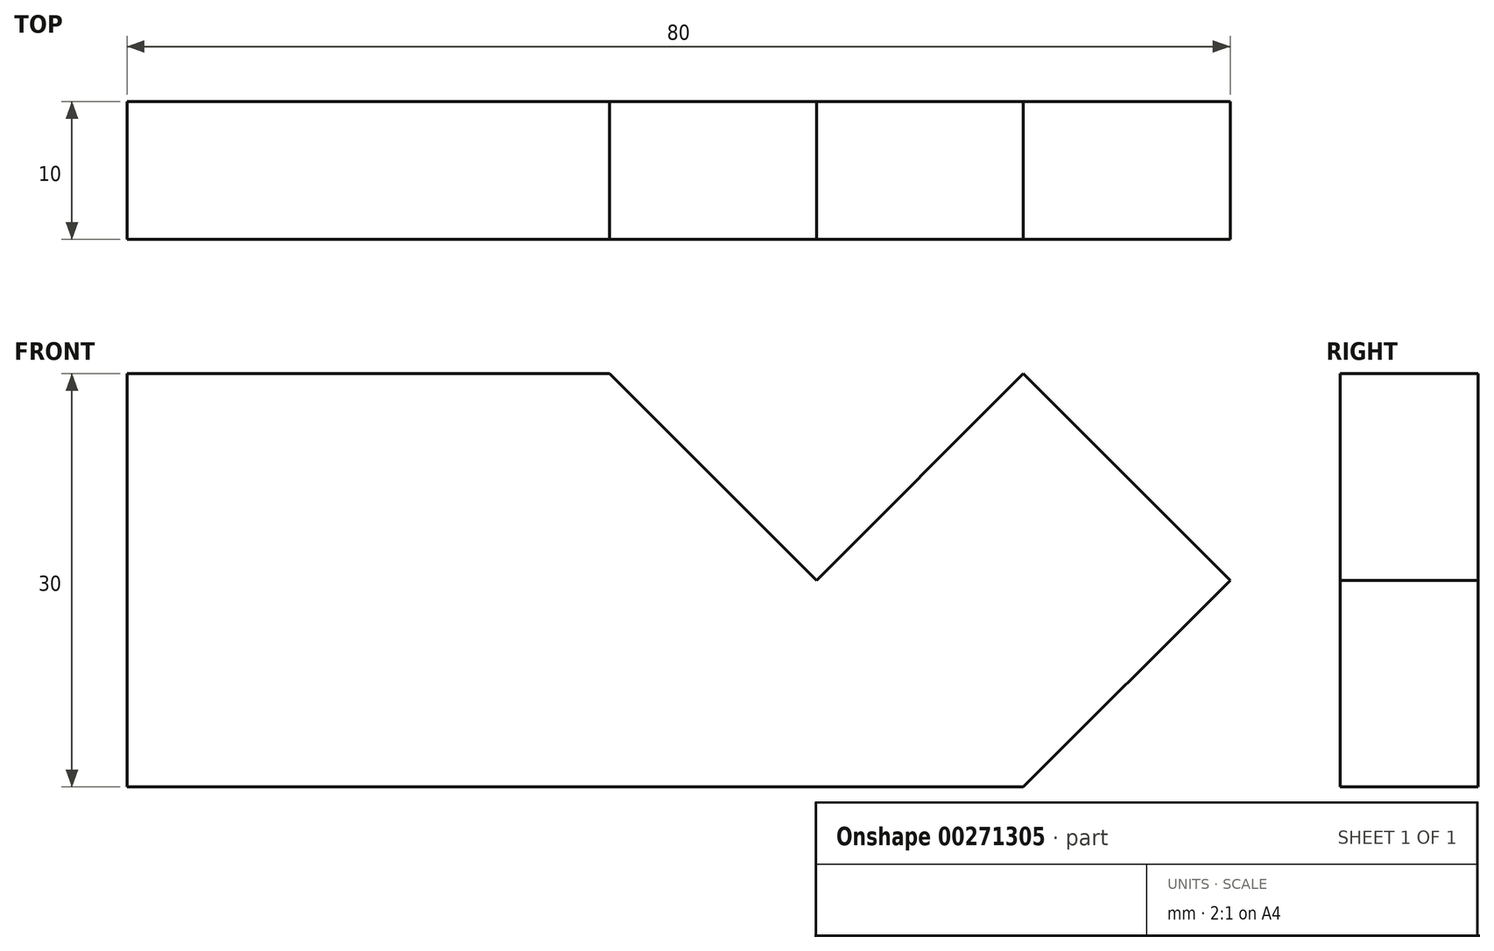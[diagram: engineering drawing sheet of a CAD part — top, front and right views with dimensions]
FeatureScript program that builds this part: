
annotation { "Feature Type Name" : "Feature", "Feature Type Description" : "" }
export const myFeature = defineFeature(function(context is Context, id is Id, definition is map)
    precondition{}
    {
        {
            var Q0;
            Q0=qCreatedBy(makeId("Front.planeOp"),FACE);
            var sketch = newSketch(context, id + "F0", { "sketchPlane" : qUnion([Q0])});
            skLineSegment(sketch, "E0", {"start": v(0, 0) * mm, "end": v(0, 35) * mm});
            skLineSegment(sketch, "E1", {"start": v(0, 35) * mm, "end": v(35, 35) * mm});
            skLineSegment(sketch, "E2", {"start": v(35, 35) * mm, "end": v(50, 20) * mm});
            skLineSegment(sketch, "E3", {"start": v(0, 5) * mm, "end": v(65, 5) * mm});
            skLineSegment(sketch, "E4", {"start": v(65, 5) * mm, "end": v(80, 20) * mm});
            skLineSegment(sketch, "E5", {"start": v(80, 20) * mm, "end": v(65, 35) * mm});
            skLineSegment(sketch, "E6", {"start": v(50, 20) * mm, "end": v(65, 35) * mm});
            skSolve(sketch);
        }
        {
            var Q0;
            Q0 = qSketchRegion(id + "F0", true);
            extrude(context, id + "F1", {"entities" : qUnion([Q0]), "depth" : 10 * mm});
        }
    });
